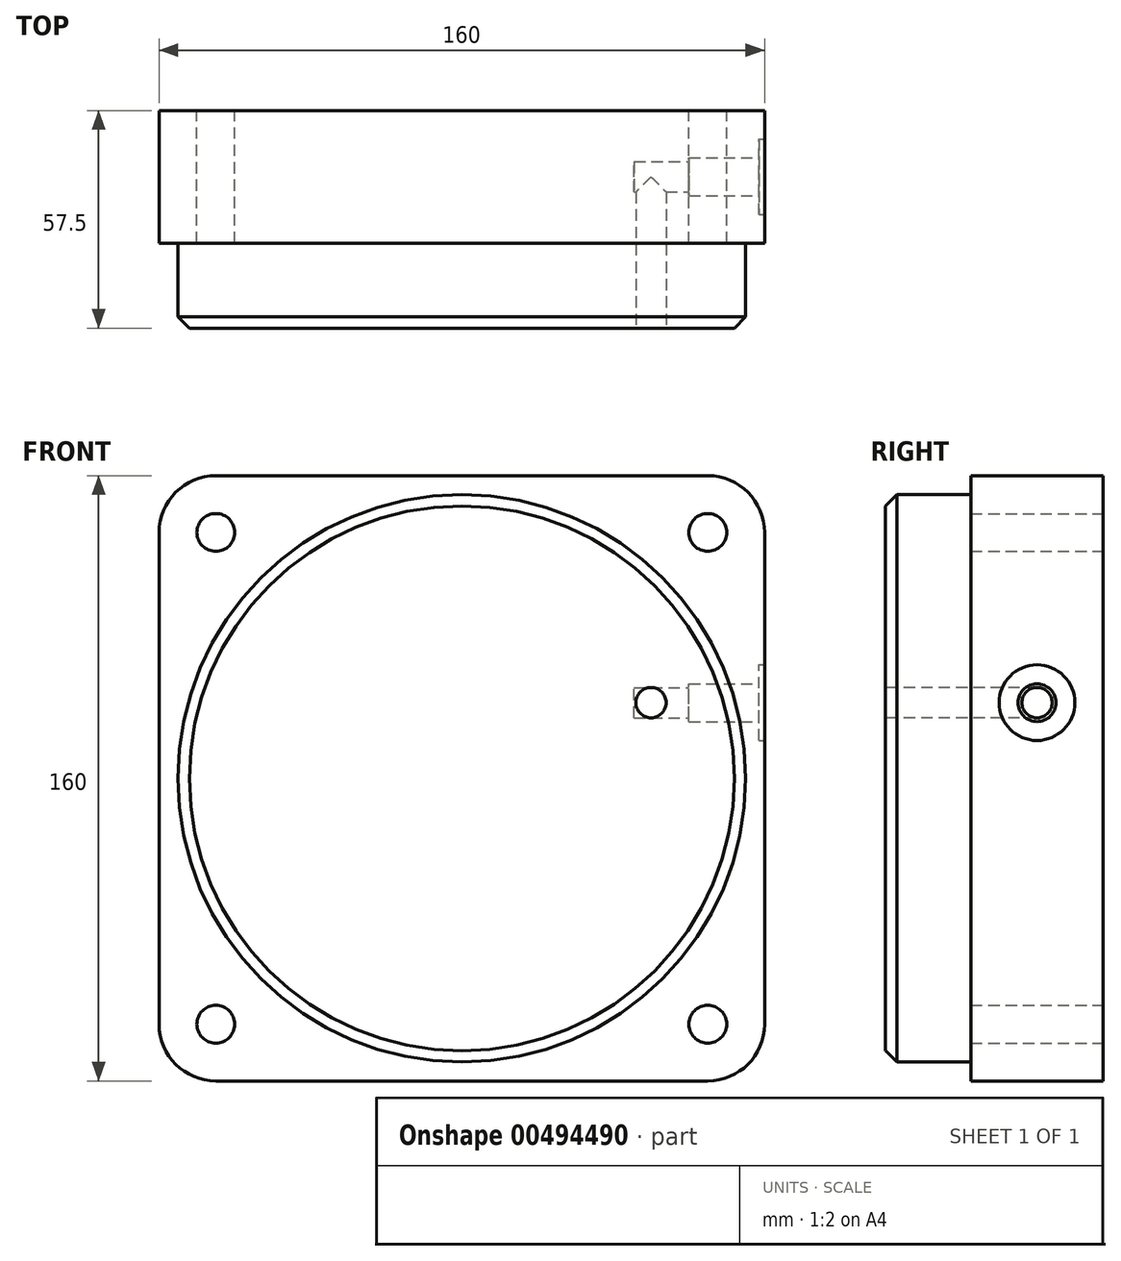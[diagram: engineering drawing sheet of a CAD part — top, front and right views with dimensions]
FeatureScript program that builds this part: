
annotation { "Feature Type Name" : "Feature", "Feature Type Description" : "" }
export const myFeature = defineFeature(function(context is Context, id is Id, definition is map)
    precondition{}
    {
        {
            var Q0;
            Q0=qCreatedBy(makeId("Front.planeOp"),FACE);
            var sketch = newSketch(context, id + "F0", { "sketchPlane" : qUnion([Q0])});
            skLineSegment(sketch, "E0.bottom", {"start": v(80, -80) * mm, "end": v(-80, -80) * mm});
            skLineSegment(sketch, "E0.top", {"start": v(80, 80) * mm, "end": v(-80, 80) * mm});
            skLineSegment(sketch, "E0.left", {"start": v(80, -80) * mm, "end": v(80, 80) * mm});
            skLineSegment(sketch, "E0.right", {"start": v(-80, -80) * mm, "end": v(-80, 80) * mm});
            skPoint(sketch, "E0.middle", {"position": v(0, 0) * mm});
            skCircle(sketch, "E1", {"center": v(0, 0) * mm, "radius": 75 * mm});
            skPoint(sketch, "E2", {"position": v(-65, 65) * mm});
            skPoint(sketch, "E3.MirrorP", {"position": v(65, 65) * mm});
            skPoint(sketch, "E4.MirrorP", {"position": v(-65, -65) * mm});
            skPoint(sketch, "E5.MirrorP", {"position": v(65, -65) * mm});
            skPoint(sketch, "E6", {"position": v(50, 20) * mm});
            skSolve(sketch);
        }
        {
            var Q0;
            Q0=makeQuery(id+"F0.imprint","IMPRINT",FACE,{"disambiguationData":[TD([[makeQuery(id+"F0.imprint","IMPRINT",EDGE,{"derivedFrom":sQuery(id+"F0.wireOp",EDGE,"E0.bottom")}),-1.0]])]});
            var Q1;
            Q1=makeQuery(id+"F0.imprint","IMPRINT",FACE,{"disambiguationData":[TD([[makeQuery(id+"F0.imprint","IMPRINT",EDGE,{"derivedFrom":sQuery(id+"F0.wireOp",EDGE,"E1")}),1.0]])]});
            extrude(context, id + "F1", {"entities" : qUnion([Q0, Q1]), "depth" : 35 * mm});
        }
        {
            var Q0;
            Q0=makeQuery(id+"F0.imprint","IMPRINT",FACE,{"disambiguationData":[TD([[makeQuery(id+"F0.imprint","IMPRINT",EDGE,{"derivedFrom":sQuery(id+"F0.wireOp",EDGE,"E1")}),1.0]])]});
            extrude(context, id + "F2", {"entities" : qUnion([Q0]), "operationType" : NewBodyOperationType.ADD, "depth" : 57.5 * mm});
        }
        {
            var Q0;
            Q0=makeQuery(id+"F2.opExtrude","CAP_EDGE",EDGE,{"disambiguationData":[OSD([sQuery(id+"F0.wireOp",EDGE,"E1")])],"isStart":false});
            chamfer(context, id + "F3", {"entities" : qUnion([Q0]), "chamferType" : ChamferType.OFFSET_ANGLE, "width" : 3 * mm, "oppositeDirection" : false, "angle" : 45 * degree, "tangentPropagation" : true});
        }
        {
            var Q0;
            Q0=makeQuery(id+"F1.opExtrude","SWEPT_EDGE",EDGE,{"disambiguationData":[OSD([sQuery(id+"F0.wireOp",EDGE,"E0.top"),sQuery(id+"F0.wireOp",EDGE,"E0.right")])]});
            var Q1;
            Q1=makeQuery(id+"F1.opExtrude","SWEPT_EDGE",EDGE,{"disambiguationData":[OSD([sQuery(id+"F0.wireOp",EDGE,"E0.bottom"),sQuery(id+"F0.wireOp",EDGE,"E0.right")])]});
            var Q2;
            Q2=makeQuery(id+"F1.opExtrude","SWEPT_EDGE",EDGE,{"disambiguationData":[OSD([sQuery(id+"F0.wireOp",EDGE,"E0.bottom"),sQuery(id+"F0.wireOp",EDGE,"E0.left")])]});
            var Q3;
            Q3=makeQuery(id+"F1.opExtrude","SWEPT_EDGE",EDGE,{"disambiguationData":[OSD([sQuery(id+"F0.wireOp",EDGE,"E0.top"),sQuery(id+"F0.wireOp",EDGE,"E0.left")])]});
            fillet(context, id + "F4", {"entities" : qUnion([Q0, Q1, Q2, Q3]), "radius" : 15 * mm, "tangentPropagation" : true, "allowEdgeOverflow" : false});
        }
        {
            var Q0;
            Q0=sQuery(id+"F0.wireOp",VERTEX,"E2");
            var Q1;
            Q1=sQuery(id+"F0.wireOp",VERTEX,"E3.MirrorP");
            var Q2;
            Q2=sQuery(id+"F0.wireOp",VERTEX,"E5.MirrorP");
            var Q3;
            Q3=sQuery(id+"F0.wireOp",VERTEX,"E4.MirrorP");
            var Q4;
            Q4=makeQuery(id+"F1.opExtrude","SWEPT_BODY",BODY,{"disambiguationData":[OSD([sQuery(id+"F0.wireOp",EDGE,"E0.bottom"),sQuery(id+"F0.wireOp",EDGE,"E0.top"),sQuery(id+"F0.wireOp",EDGE,"E0.left"),sQuery(id+"F0.wireOp",EDGE,"E0.right")])]});
            hole(context, id + "F5", {"style" : HoleStyle.SIMPLE, "endStyle" : HoleEndStyle.THROUGH, "oppositeDirection" : true, "holeDiameter" : 10 * mm, "isTappedThrough" : true, "tappedDepth" : 12 * mm, "tapClearance" : 3, "locations" : qUnion([Q0, Q1, Q2, Q3]), "scope" : qUnion([Q4])});
        }
        {
            var Q0;
            Q0=makeQuery(id+"F2.opExtrude","CAP_FACE",FACE,{"disambiguationData":[OSD([sQuery(id+"F0.wireOp",EDGE,"E1")])],"isStart":false});
            var sketch = newSketch(context, id + "F6", { "sketchPlane" : qUnion([Q0])});
            skPoint(sketch, "E7", {"position": v(50, 20) * mm});
            skSolve(sketch);
        }
        {
            var Q0;
            Q0=sQuery(id+"F6.wireOp",VERTEX,"E7");
            var Q1;
            Q1=makeQuery(id+"F1.opExtrude","SWEPT_BODY",BODY,{"disambiguationData":[OSD([sQuery(id+"F0.wireOp",EDGE,"E0.bottom"),sQuery(id+"F0.wireOp",EDGE,"E0.top"),sQuery(id+"F0.wireOp",EDGE,"E0.left"),sQuery(id+"F0.wireOp",EDGE,"E0.right")])]});
            hole(context, id + "F7", {"style" : HoleStyle.SIMPLE, "endStyle" : HoleEndStyle.BLIND, "holeDiameter" : 8 * mm, "holeDepth" : 40 * mm, "isTappedThrough" : true, "tappedDepth" : 12 * mm, "tapClearance" : 3, "locations" : qUnion([Q0]), "scope" : qUnion([Q1])});
        }
        {
            var Q0;
            Q0=makeQuery(id+"F1.opExtrude","SWEPT_FACE",FACE,{"disambiguationData":[OSD([sQuery(id+"F0.wireOp",EDGE,"E0.left")])]});
            var sketch = newSketch(context, id + "F8", { "sketchPlane" : qUnion([Q0])});
            skPoint(sketch, "E8", {"position": v(-17.5, 20) * mm});
            skCircle(sketch, "E9", {"center": v(-17.5, 20) * mm, "radius": 4 * mm});
            skCircle(sketch, "E10", {"center": v(-17.5, 20) * mm, "radius": 5 * mm});
            skCircle(sketch, "E11", {"center": v(-17.5, 20) * mm, "radius": 10 * mm});
            skSolve(sketch);
        }
        {
            var Q0;
            Q0=makeQuery(id+"F8.imprint","IMPRINT",FACE,{"disambiguationData":[TD([[makeQuery(id+"F8.imprint","IMPRINT",EDGE,{"derivedFrom":sQuery(id+"F8.wireOp",EDGE,"E9")}),1.0]])]});
            extrude(context, id + "F9", {"entities" : qUnion([Q0]), "operationType" : NewBodyOperationType.REMOVE, "oppositeDirection" : true, "depth" : 34.5 * mm});
        }
        {
            var Q0;
            Q0=makeQuery(id+"F8.imprint","IMPRINT",FACE,{"disambiguationData":[TD([[makeQuery(id+"F8.imprint","IMPRINT",EDGE,{"derivedFrom":sQuery(id+"F8.wireOp",EDGE,"E9")}),-1.0]])]});
            extrude(context, id + "F10", {"entities" : qUnion([Q0]), "operationType" : NewBodyOperationType.REMOVE, "oppositeDirection" : true, "depth" : 20 * mm});
        }
        {
            var Q0;
            Q0=makeQuery(id+"F8.imprint","IMPRINT",FACE,{"disambiguationData":[TD([[makeQuery(id+"F8.imprint","IMPRINT",EDGE,{"derivedFrom":sQuery(id+"F8.wireOp",EDGE,"E10")}),-1.0]])]});
            extrude(context, id + "F11", {"entities" : qUnion([Q0]), "operationType" : NewBodyOperationType.REMOVE, "oppositeDirection" : true, "depth" : 1.5 * mm});
        }
    });
